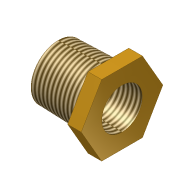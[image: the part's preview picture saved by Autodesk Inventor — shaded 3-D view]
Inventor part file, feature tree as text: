
AUTODESK INVENTOR PART (.ipt)
format: ipt  version: Autodesk Inventor 10  size: 181,248 bytes
history: native  units: mm (DEFAULTED — no unit token found)
features: thread x4, sketch x1, imported_body x1
ambient origin geometry x8: Origin, YZ Plane, XZ Plane, XY Plane, X Axis, Y Axis, Z Axis, Center Point
feature tree (6):
  sketch  "Sketch1"
  imported_body  "Base1"
  thread  "Thread1"  [1 undecoded]
  thread  "Thread2"  [1 undecoded]
  thread  "Thread3"  [1 undecoded]
  thread  "Thread4"  [1 undecoded]
note: 4 required parameter values undecoded (feature->parameter linkage not recoverable at this tier; creation-order binding heuristic only, values carry confidence <= 0.55)
